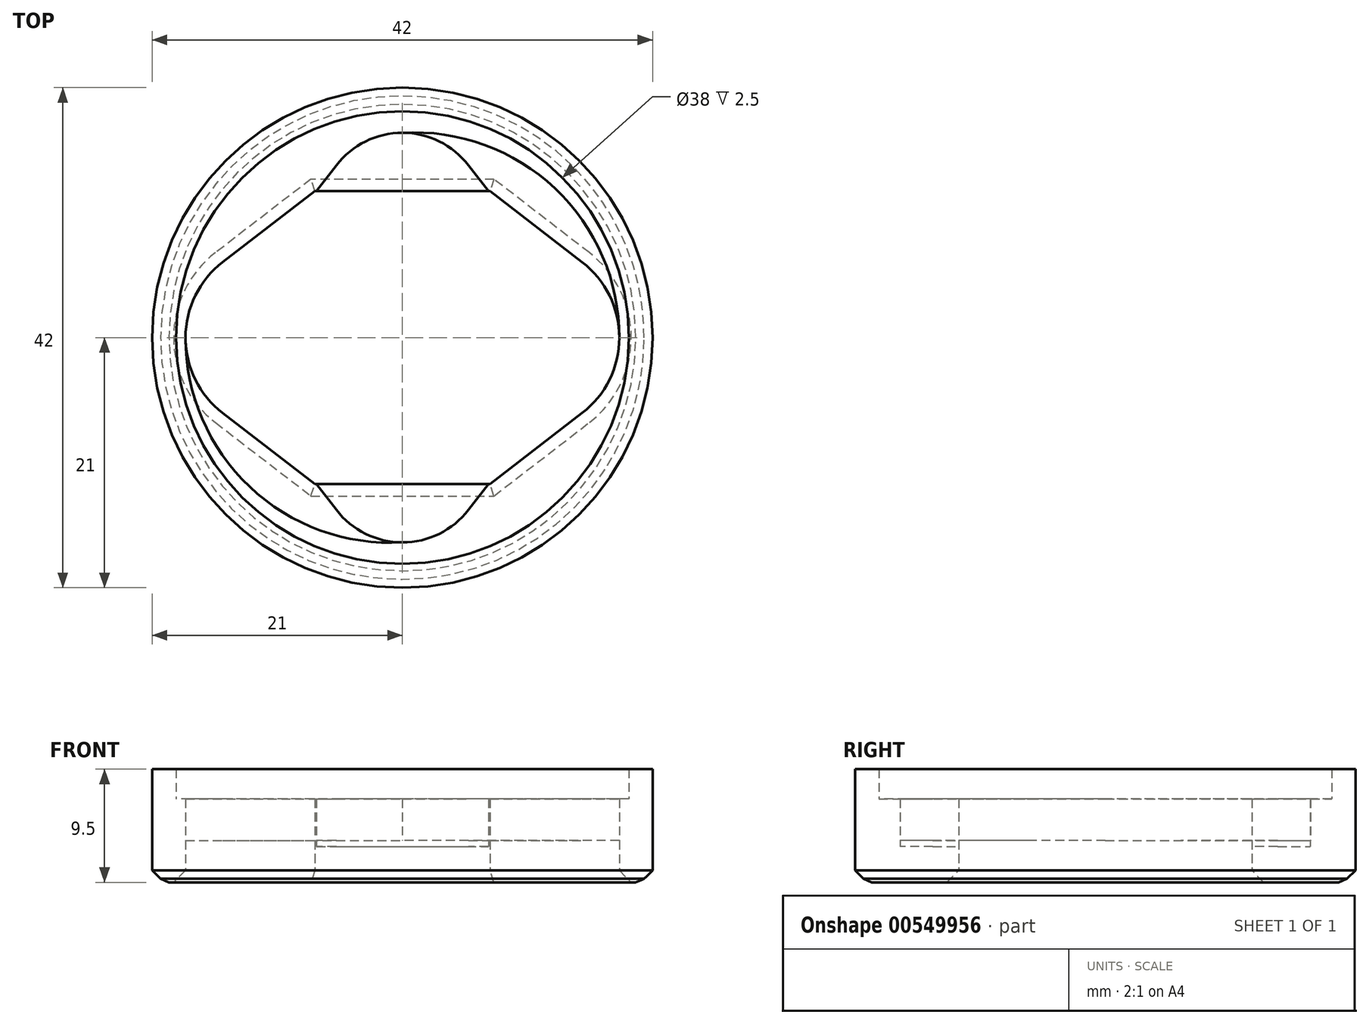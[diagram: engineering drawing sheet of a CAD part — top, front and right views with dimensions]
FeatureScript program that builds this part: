
annotation { "Feature Type Name" : "Feature", "Feature Type Description" : "" }
export const myFeature = defineFeature(function(context is Context, id is Id, definition is map)
    precondition{}
    {
        {
            var Q0;
            Q0=qCreatedBy(makeId("Top.planeOp"),FACE);
            var sketch = newSketch(context, id + "F0", { "sketchPlane" : qUnion([Q0])});
            skCircle(sketch, "E0", {"center": v(0, 0) * mm, "radius": 21 * mm});
            skLineSegment(sketch, "E1", {"start": v(-7, 11.3) * mm, "end": v(7, 11.3) * mm});
            skLineSegment(sketch, "E2", {"start": v(7, 11.3) * mm, "end": v(14.47, 5.55) * mm});
            skLineSegment(sketch, "E3", {"start": v(-7, 11.3) * mm, "end": v(-14.47, 5.55) * mm});
            skLineSegment(sketch, "E4", {"start": v(-14.47, -5.55) * mm, "end": v(-7, -11.3) * mm});
            skLineSegment(sketch, "E5", {"start": v(-7, -11.3) * mm, "end": v(7, -11.3) * mm});
            skLineSegment(sketch, "E6", {"start": v(7, -11.3) * mm, "end": v(14.47, -5.55) * mm});
            skArc(sketch, "E7", {"start": v(-14.47, 5.55) * mm, "mid": v(-17.2, 0) * mm, "end": v(-14.47, -5.55) * mm});
            skArc(sketch, "E8", {"start": v(14.47, -5.55) * mm, "mid": v(17.2, 0) * mm, "end": v(14.47, 5.55) * mm});
            skLineSegment(sketch, "E9.0", {"start": v(-7.34, 12.3) * mm, "end": v(7.34, 12.3) * mm});
            skLineSegment(sketch, "E9.1", {"start": v(7.34, 12.3) * mm, "end": v(15.08, 6.34) * mm});
            skLineSegment(sketch, "E9.2", {"start": v(-7.34, 12.3) * mm, "end": v(-15.08, 6.34) * mm});
            skArc(sketch, "E9.3", {"start": v(15.08, -6.34) * mm, "mid": v(18.2, 0) * mm, "end": v(15.08, 6.34) * mm});
            skArc(sketch, "E9.4", {"start": v(-15.08, 6.34) * mm, "mid": v(-18.2, 0) * mm, "end": v(-15.08, -6.34) * mm});
            skLineSegment(sketch, "E9.5", {"start": v(-15.08, -6.34) * mm, "end": v(-7.34, -12.3) * mm});
            skLineSegment(sketch, "E9.6", {"start": v(-7.34, -12.3) * mm, "end": v(7.34, -12.3) * mm});
            skLineSegment(sketch, "E9.7", {"start": v(7.34, -12.3) * mm, "end": v(15.08, -6.34) * mm});
            skSolve(sketch);
        }
        {
            var Q0;
            Q0 = qSketchRegion(id + "F0", true);
            extrude(context, id + "F1", {"entities" : qUnion([Q0]), "depth" : 3 * mm, "offsetDistance" : 25 * mm});
        }
        {
            var Q0;
            Q0=makeQuery(id+"F1.opExtrude","CAP_FACE",FACE,{"disambiguationData":[OSD([sQuery(id+"F0.wireOp",EDGE,"E0"),sQuery(id+"F0.wireOp",EDGE,"E9.0"),sQuery(id+"F0.wireOp",EDGE,"E9.1"),sQuery(id+"F0.wireOp",EDGE,"E9.2"),sQuery(id+"F0.wireOp",EDGE,"E9.3"),sQuery(id+"F0.wireOp",EDGE,"E9.4"),sQuery(id+"F0.wireOp",EDGE,"E9.5"),sQuery(id+"F0.wireOp",EDGE,"E9.6"),sQuery(id+"F0.wireOp",EDGE,"E9.7")])],"isStart":false});
            var sketch = newSketch(context, id + "F2", { "sketchPlane" : qUnion([Q0])});
            skLineSegment(sketch, "E10", {"start": v(-5.55, -14.47) * mm, "end": v(-11.3, -7) * mm, "construction": true});
            skLineSegment(sketch, "E11", {"start": v(-11.3, -7) * mm, "end": v(-11.3, 7) * mm, "construction": true});
            skLineSegment(sketch, "E12", {"start": v(-11.3, 7) * mm, "end": v(-5.55, 14.47) * mm, "construction": true});
            skLineSegment(sketch, "E13", {"start": v(5.55, 14.47) * mm, "end": v(11.3, 7) * mm, "construction": true});
            skLineSegment(sketch, "E14", {"start": v(11.3, 7) * mm, "end": v(11.3, -7) * mm, "construction": true});
            skLineSegment(sketch, "E15", {"start": v(11.3, -7) * mm, "end": v(5.55, -14.47) * mm, "construction": true});
            skArc(sketch, "E16", {"start": v(5.55, 14.47) * mm, "mid": v(0, 17.2) * mm, "end": v(-5.55, 14.47) * mm, "construction": true});
            skArc(sketch, "E17", {"start": v(-5.55, -14.47) * mm, "mid": v(0, -17.2) * mm, "end": v(5.55, -14.47) * mm, "construction": true});
            skLineSegment(sketch, "E18", {"start": v(-9.43, 9.43) * mm, "end": v(-5.55, 14.47) * mm, "construction": true});
            skLineSegment(sketch, "E19", {"start": v(9.43, -9.43) * mm, "end": v(5.55, -14.47) * mm, "construction": true});
            skLineSegment(sketch, "E20", {"start": v(-7.34, 12.3) * mm, "end": v(-7.22, 12.3) * mm});
            skLineSegment(sketch, "E21", {"start": v(-7.22, 12.3) * mm, "end": v(-5.55, 14.47) * mm});
            skArc(sketch, "E22", {"start": v(0, 17.2) * mm, "mid": v(-3.1, 16.48) * mm, "end": v(-5.55, 14.47) * mm});
            skArc(sketch, "E23", {"start": v(15.08, -6.34) * mm, "mid": v(17.38, -3.53) * mm, "end": v(18.2, 0) * mm});
            skLineSegment(sketch, "E24", {"start": v(15.08, -6.34) * mm, "end": v(7.34, -12.3) * mm});
            skLineSegment(sketch, "E25", {"start": v(7.34, -12.3) * mm, "end": v(7.22, -12.3) * mm});
            skLineSegment(sketch, "E26", {"start": v(7.22, -12.3) * mm, "end": v(5.55, -14.47) * mm});
            skArc(sketch, "E27", {"start": v(0, -17.2) * mm, "mid": v(3.1, -16.48) * mm, "end": v(5.55, -14.47) * mm});
            skArc(sketch, "E28", {"start": v(-15.08, 6.34) * mm, "mid": v(-17.38, 3.53) * mm, "end": v(-18.2, 0) * mm});
            skLineSegment(sketch, "E29", {"start": v(-15.08, 6.34) * mm, "end": v(-7.34, 12.3) * mm});
            skArc(sketch, "E30", {"start": v(5.55, 14.47) * mm, "mid": v(3.1, 16.48) * mm, "end": v(0, 17.2) * mm});
            skLineSegment(sketch, "E31", {"start": v(5.55, 14.47) * mm, "end": v(7.22, 12.3) * mm});
            skLineSegment(sketch, "E32", {"start": v(7.22, 12.3) * mm, "end": v(7.34, 12.3) * mm});
            skLineSegment(sketch, "E33", {"start": v(7.34, 12.3) * mm, "end": v(15.08, 6.34) * mm});
            skArc(sketch, "E34", {"start": v(18.2, 0) * mm, "mid": v(17.38, 3.53) * mm, "end": v(15.08, 6.34) * mm});
            skArc(sketch, "E35", {"start": v(-5.55, -14.47) * mm, "mid": v(-3.1, -16.48) * mm, "end": v(0, -17.2) * mm});
            skLineSegment(sketch, "E36", {"start": v(-5.55, -14.47) * mm, "end": v(-7.22, -12.3) * mm});
            skLineSegment(sketch, "E37", {"start": v(-7.22, -12.3) * mm, "end": v(-7.34, -12.3) * mm});
            skLineSegment(sketch, "E38", {"start": v(-7.34, -12.3) * mm, "end": v(-15.08, -6.34) * mm});
            skArc(sketch, "E39", {"start": v(-18.2, 0) * mm, "mid": v(-17.38, -3.53) * mm, "end": v(-15.08, -6.34) * mm});
            skSolve(sketch);
        }
        {
            var Q0;
            Q0=makeQuery(id+"F2.imprint","IMPRINT",FACE,{"disambiguationData":[TD([[makeQuery(id+"F2.imprint","IMPRINT",EDGE,{"derivedFrom":sQuery(id+"F2.wireOp",EDGE,"E20")}),1.0]])]});
            extrude(context, id + "F3", {"entities" : qUnion([Q0]), "operationType" : NewBodyOperationType.ADD, "depth" : 0.5 * mm, "offsetDistance" : 25 * mm});
        }
        {
            var Q0;
            Q0=makeQuery(id+"F3.opExtrude","CAP_FACE",FACE,{"disambiguationData":[OSD([sQuery(id+"F0.wireOp",EDGE,"E0"),sQuery(id+"F2.wireOp",EDGE,"E20"),sQuery(id+"F2.wireOp",EDGE,"E21"),sQuery(id+"F2.wireOp",EDGE,"E22"),sQuery(id+"F2.wireOp",EDGE,"E23"),sQuery(id+"F2.wireOp",EDGE,"E24"),sQuery(id+"F2.wireOp",EDGE,"E25"),sQuery(id+"F2.wireOp",EDGE,"E26"),sQuery(id+"F2.wireOp",EDGE,"E27"),sQuery(id+"F2.wireOp",EDGE,"E28"),sQuery(id+"F2.wireOp",EDGE,"E29"),sQuery(id+"F2.wireOp",EDGE,"E30"),sQuery(id+"F2.wireOp",EDGE,"E31"),sQuery(id+"F2.wireOp",EDGE,"E32"),sQuery(id+"F2.wireOp",EDGE,"E33"),sQuery(id+"F2.wireOp",EDGE,"E34"),sQuery(id+"F2.wireOp",EDGE,"E35"),sQuery(id+"F2.wireOp",EDGE,"E36"),sQuery(id+"F2.wireOp",EDGE,"E37"),sQuery(id+"F2.wireOp",EDGE,"E38"),sQuery(id+"F2.wireOp",EDGE,"E39")])],"isStart":false});
            var sketch = newSketch(context, id + "F4", { "sketchPlane" : qUnion([Q0])});
            skLineSegment(sketch, "E40", {"start": v(-5.55, -14.47) * mm, "end": v(-11.3, -7) * mm, "construction": true});
            skLineSegment(sketch, "E41", {"start": v(-11.3, -7) * mm, "end": v(-11.3, 7) * mm, "construction": true});
            skLineSegment(sketch, "E42", {"start": v(-11.3, 7) * mm, "end": v(-5.55, 14.47) * mm, "construction": true});
            skLineSegment(sketch, "E43", {"start": v(5.55, 14.47) * mm, "end": v(11.3, 7) * mm, "construction": true});
            skLineSegment(sketch, "E44", {"start": v(11.3, 7) * mm, "end": v(11.3, -7) * mm, "construction": true});
            skLineSegment(sketch, "E45", {"start": v(11.3, -7) * mm, "end": v(5.55, -14.47) * mm, "construction": true});
            skArc(sketch, "E46", {"start": v(5.55, 14.47) * mm, "mid": v(0, 17.2) * mm, "end": v(-5.55, 14.47) * mm, "construction": true});
            skArc(sketch, "E47", {"start": v(-5.55, -14.47) * mm, "mid": v(0, -17.2) * mm, "end": v(5.55, -14.47) * mm, "construction": true});
            skLineSegment(sketch, "E48", {"start": v(-9.43, 9.43) * mm, "end": v(-5.55, 14.47) * mm, "construction": true});
            skLineSegment(sketch, "E49", {"start": v(9.43, -9.43) * mm, "end": v(5.55, -14.47) * mm, "construction": true});
            skLineSegment(sketch, "E50", {"start": v(-7.34, 12.3) * mm, "end": v(-7.22, 12.3) * mm});
            skLineSegment(sketch, "E51", {"start": v(-7.22, 12.3) * mm, "end": v(-5.55, 14.47) * mm});
            skArc(sketch, "E52", {"start": v(0, 17.2) * mm, "mid": v(-3.1, 16.48) * mm, "end": v(-5.55, 14.47) * mm});
            skArc(sketch, "E53", {"start": v(15.08, -6.34) * mm, "mid": v(17.38, -3.53) * mm, "end": v(18.2, 0) * mm});
            skLineSegment(sketch, "E54", {"start": v(15.08, -6.34) * mm, "end": v(7.34, -12.3) * mm});
            skLineSegment(sketch, "E55", {"start": v(7.34, -12.3) * mm, "end": v(7.22, -12.3) * mm});
            skLineSegment(sketch, "E56", {"start": v(7.22, -12.3) * mm, "end": v(5.55, -14.47) * mm});
            skArc(sketch, "E57", {"start": v(0, -17.2) * mm, "mid": v(3.1, -16.48) * mm, "end": v(5.55, -14.47) * mm});
            skArc(sketch, "E58", {"start": v(18.2, 0) * mm, "mid": v(12.81, 12.53) * mm, "end": v(0, 17.2) * mm});
            skArc(sketch, "E59", {"start": v(-18.2, 0) * mm, "mid": v(-12.81, -12.53) * mm, "end": v(0, -17.2) * mm});
            skArc(sketch, "E60", {"start": v(-15.08, 6.34) * mm, "mid": v(-17.38, 3.53) * mm, "end": v(-18.2, 0) * mm});
            skLineSegment(sketch, "E61", {"start": v(-15.08, 6.34) * mm, "end": v(-7.34, 12.3) * mm});
            skSolve(sketch);
        }
        {
            var Q0;
            Q0=makeQuery(id+"F4.imprint","IMPRINT",FACE,{"disambiguationData":[TD([[makeQuery(id+"F4.imprint","IMPRINT",EDGE,{"derivedFrom":sQuery(id+"F4.wireOp",EDGE,"E50")}),1.0]])]});
            extrude(context, id + "F5", {"entities" : qUnion([Q0]), "operationType" : NewBodyOperationType.ADD, "depth" : 3.5 * mm, "offsetDistance" : 25 * mm});
        }
        {
            var Q0;
            Q0=makeQuery(id+"F5.opExtrude","CAP_FACE",FACE,{"disambiguationData":[OSD([sQuery(id+"F0.wireOp",EDGE,"E0"),sQuery(id+"F4.wireOp",EDGE,"E50"),sQuery(id+"F4.wireOp",EDGE,"E51"),sQuery(id+"F4.wireOp",EDGE,"E52"),sQuery(id+"F4.wireOp",EDGE,"E53"),sQuery(id+"F4.wireOp",EDGE,"E54"),sQuery(id+"F4.wireOp",EDGE,"E55"),sQuery(id+"F4.wireOp",EDGE,"E56"),sQuery(id+"F4.wireOp",EDGE,"E57"),sQuery(id+"F4.wireOp",EDGE,"E58"),sQuery(id+"F4.wireOp",EDGE,"E59"),sQuery(id+"F4.wireOp",EDGE,"E60"),sQuery(id+"F4.wireOp",EDGE,"E61")])],"isStart":false});
            var sketch = newSketch(context, id + "F6", { "sketchPlane" : qUnion([Q0])});
            skCircle(sketch, "E62", {"center": v(0, 0) * mm, "radius": 19 * mm});
            skSolve(sketch);
        }
        {
            var Q0;
            Q0=makeQuery(id+"F6.imprint","IMPRINT",FACE,{"disambiguationData":[TD([[makeQuery(id+"F6.imprint","IMPRINT",EDGE,{"derivedFrom":sQuery(id+"F6.wireOp",EDGE,"E62")}),-1.0]])]});
            extrude(context, id + "F7", {"entities" : qUnion([Q0]), "operationType" : NewBodyOperationType.ADD, "depth" : 2.5 * mm, "offsetDistance" : 25 * mm});
        }
        {
            var Q0;
            Q0=makeQuery(id+"F1.opExtrude","CAP_EDGE",EDGE,{"disambiguationData":[OSD([sQuery(id+"F0.wireOp",EDGE,"E0")])],"isStart":true});
            chamfer(context, id + "F8", {"entities" : qUnion([Q0]), "width" : 1 * mm, "tangentPropagation" : true});
        }
        {
            var Q0;
            Q0=makeQuery(id+"F1.opExtrude","CAP_FACE",FACE,{"disambiguationData":[OSD([sQuery(id+"F0.wireOp",EDGE,"E0"),sQuery(id+"F0.wireOp",EDGE,"E9.0"),sQuery(id+"F0.wireOp",EDGE,"E9.1"),sQuery(id+"F0.wireOp",EDGE,"E9.2"),sQuery(id+"F0.wireOp",EDGE,"E9.3"),sQuery(id+"F0.wireOp",EDGE,"E9.4"),sQuery(id+"F0.wireOp",EDGE,"E9.5"),sQuery(id+"F0.wireOp",EDGE,"E9.6"),sQuery(id+"F0.wireOp",EDGE,"E9.7")])],"isStart":true});
            chamfer(context, id + "F9", {"entities" : qUnion([Q0]), "width" : 1 * mm, "tangentPropagation" : true});
        }
    });
